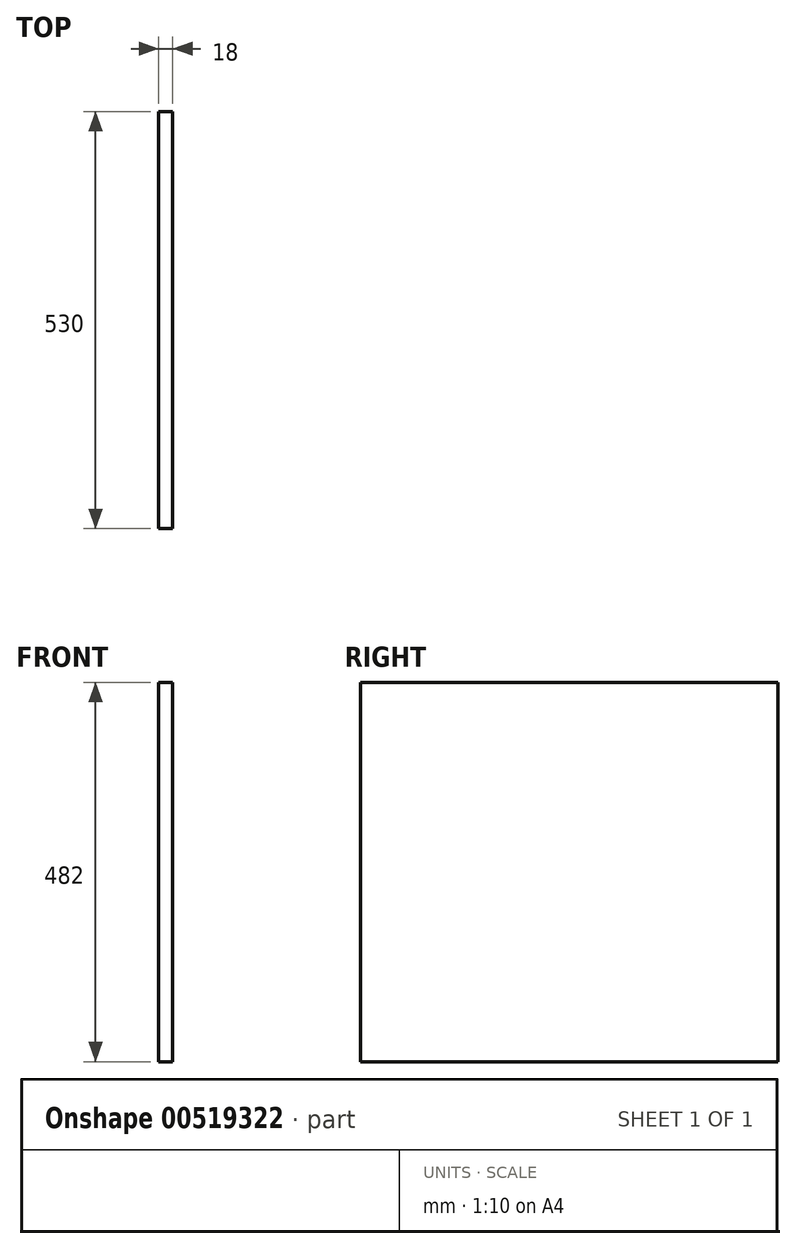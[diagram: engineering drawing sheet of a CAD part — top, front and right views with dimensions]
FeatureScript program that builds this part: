
annotation { "Feature Type Name" : "Feature", "Feature Type Description" : "" }
export const myFeature = defineFeature(function(context is Context, id is Id, definition is map)
    precondition{}
    {
        {
            var Q0;
            Q0=qCreatedBy(makeId("Right.planeOp"),FACE);
            var sketch = newSketch(context, id + "F0", { "sketchPlane" : qUnion([Q0])});
            skLineSegment(sketch, "E0.bottom", {"start": v(265, 241) * mm, "end": v(-265, 241) * mm});
            skLineSegment(sketch, "E0.top", {"start": v(265, -241) * mm, "end": v(-265, -241) * mm});
            skLineSegment(sketch, "E0.left", {"start": v(265, 241) * mm, "end": v(265, -241) * mm});
            skLineSegment(sketch, "E0.right", {"start": v(-265, 241) * mm, "end": v(-265, -241) * mm});
            skPoint(sketch, "E0.middle", {"position": v(0, 0) * mm});
            skSolve(sketch);
        }
        {
            var Q0;
            Q0 = qSketchRegion(id + "F0", true);
            extrude(context, id + "F1", {"entities" : qUnion([Q0]), "depth" : 18 * mm, "offsetDistance" : 25 * mm});
        }
    });
